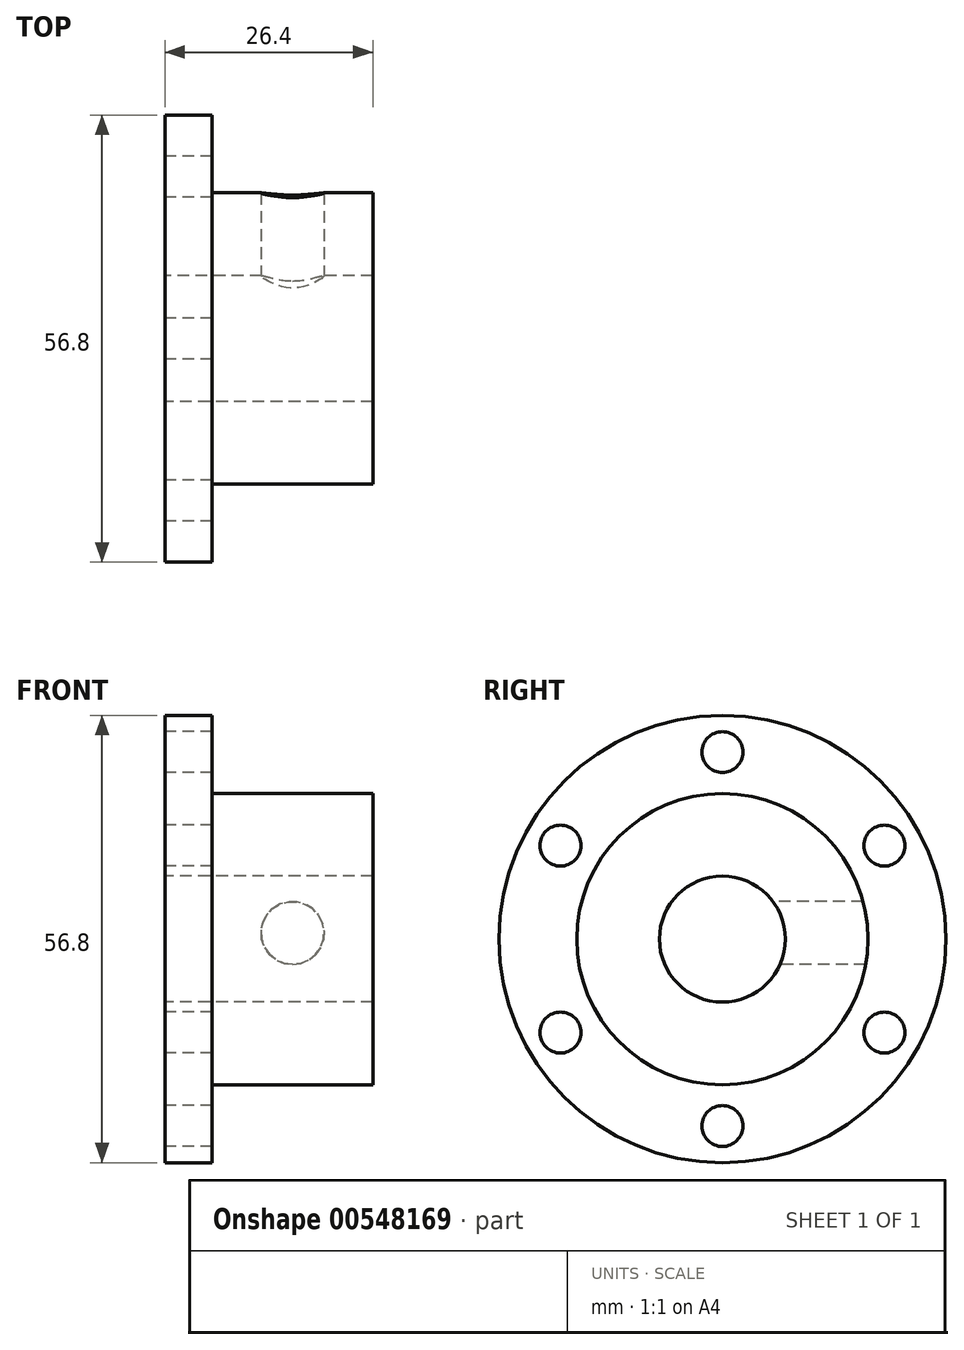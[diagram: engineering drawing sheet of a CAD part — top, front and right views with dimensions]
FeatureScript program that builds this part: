
annotation { "Feature Type Name" : "Feature", "Feature Type Description" : "" }
export const myFeature = defineFeature(function(context is Context, id is Id, definition is map)
    precondition{}
    {
        {
            var Q0;
            Q0=qCreatedBy(makeId("Front.planeOp"),FACE);
            var sketch = newSketch(context, id + "F0", { "sketchPlane" : qUnion([Q0])});
            skLineSegment(sketch, "E0", {"start": v(8.2, -2.84) * mm, "end": v(-18.2, -2.84) * mm});
            skLineSegment(sketch, "E1", {"start": v(-18.2, -2.84) * mm, "end": v(-18.2, 17.56) * mm});
            skLineSegment(sketch, "E2", {"start": v(-18.2, 17.56) * mm, "end": v(-12.2, 17.56) * mm});
            skLineSegment(sketch, "E3", {"start": v(-12.2, 17.56) * mm, "end": v(-12.2, 7.66) * mm});
            skLineSegment(sketch, "E4", {"start": v(-12.2, 7.66) * mm, "end": v(8.2, 7.66) * mm});
            skLineSegment(sketch, "E5", {"start": v(8.2, 7.66) * mm, "end": v(8.2, -2.84) * mm});
            skLineSegment(sketch, "E6", {"start": v(-18.2, -10.84) * mm, "end": v(24.04, -10.84) * mm});
            skSolve(sketch);
        }
        {
            var Q0;
            Q0=makeQuery(id+"F0.imprint","IMPRINT",FACE,{"disambiguationData":[TD([[makeQuery(id+"F0.imprint","IMPRINT",EDGE,{"derivedFrom":sQuery(id+"F0.wireOp",EDGE,"E0")}),-1.0]])]});
            var Q1;
            Q1=sQuery(id+"F0.wireOp",EDGE,"E6");
            revolve(context, id + "F1", {"entities" : qUnion([Q0]), "axis" : qUnion([Q1]), "revolveType" : RevolveType.FULL});
        }
        {
            var Q0;
            Q0=makeQuery(id+"F1.opRevolve","SWEPT_FACE",FACE,{"disambiguationData":[OSD([sQuery(id+"F0.wireOp",EDGE,"E1")])]});
            var sketch = newSketch(context, id + "F2", { "sketchPlane" : qUnion([Q0])});
            skCircle(sketch, "E7", {"center": v(0, -10.84) * mm, "radius": 23.75 * mm, "construction": true});
            skCircle(sketch, "E8", {"center": v(0, 12.9) * mm, "radius": 2.6 * mm});
            skCircle(sketch, "E9.1.0", {"center": v(-20.57, 1.03) * mm, "radius": 2.6 * mm});
            skCircle(sketch, "E9.2.0", {"center": v(-20.57, -22.72) * mm, "radius": 2.6 * mm});
            skCircle(sketch, "E9.3.0", {"center": v(0, -34.6) * mm, "radius": 2.6 * mm});
            skCircle(sketch, "E9.4.0", {"center": v(20.57, -22.72) * mm, "radius": 2.6 * mm});
            skCircle(sketch, "E9.5.0", {"center": v(20.57, 1.03) * mm, "radius": 2.6 * mm});
            skSolve(sketch);
        }
        {
            var Q0;
            Q0=makeQuery(id+"F2.imprint","IMPRINT",FACE,{"disambiguationData":[TD([[makeQuery(id+"F2.imprint","IMPRINT",EDGE,{"derivedFrom":sQuery(id+"F2.wireOp",EDGE,"E8")}),1.0]])]});
            var Q1;
            Q1=makeQuery(id+"F2.imprint","IMPRINT",FACE,{"disambiguationData":[TD([[makeQuery(id+"F2.imprint","IMPRINT",EDGE,{"derivedFrom":sQuery(id+"F2.wireOp",EDGE,"E9.1.0")}),1.0]])]});
            var Q2;
            Q2=makeQuery(id+"F2.imprint","IMPRINT",FACE,{"disambiguationData":[TD([[makeQuery(id+"F2.imprint","IMPRINT",EDGE,{"derivedFrom":sQuery(id+"F2.wireOp",EDGE,"E9.2.0")}),1.0]])]});
            var Q3;
            Q3=makeQuery(id+"F2.imprint","IMPRINT",FACE,{"disambiguationData":[TD([[makeQuery(id+"F2.imprint","IMPRINT",EDGE,{"derivedFrom":sQuery(id+"F2.wireOp",EDGE,"E9.3.0")}),1.0]])]});
            var Q4;
            Q4=makeQuery(id+"F2.imprint","IMPRINT",FACE,{"disambiguationData":[TD([[makeQuery(id+"F2.imprint","IMPRINT",EDGE,{"derivedFrom":sQuery(id+"F2.wireOp",EDGE,"E9.4.0")}),1.0]])]});
            var Q5;
            Q5=makeQuery(id+"F2.imprint","IMPRINT",FACE,{"disambiguationData":[TD([[makeQuery(id+"F2.imprint","IMPRINT",EDGE,{"derivedFrom":sQuery(id+"F2.wireOp",EDGE,"E9.5.0")}),1.0]])]});
            var Q6;
            Q6=sQuery(id+"F2.wireOp",EDGE,"E8");
            extrude(context, id + "F3", {"entities" : qUnion([Q0, Q1, Q2, Q3, Q4, Q5]), "operationType" : NewBodyOperationType.REMOVE, "surfaceEntities" : qUnion([Q6]), "oppositeDirection" : true, "depth" : 25 * mm, "offsetDistance" : 25 * mm});
        }
        {
            var Q0;
            Q0=qCreatedBy(makeId("Front.planeOp"),FACE);
            var sketch = newSketch(context, id + "F4", { "sketchPlane" : qUnion([Q0])});
            skCircle(sketch, "E10", {"center": v(-2, -10.07) * mm, "radius": 4 * mm});
            skSolve(sketch);
        }
        {
            var Q0;
            Q0 = qSketchRegion(id + "F4", true);
            extrude(context, id + "F5", {"entities" : qUnion([Q0]), "operationType" : NewBodyOperationType.REMOVE, "oppositeDirection" : true, "depth" : 25 * mm, "offsetDistance" : 25 * mm});
        }
    });
